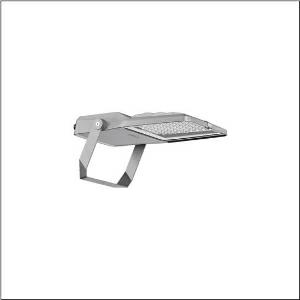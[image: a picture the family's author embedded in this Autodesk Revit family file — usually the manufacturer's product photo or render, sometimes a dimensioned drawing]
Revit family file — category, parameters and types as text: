
# Revit family: floodlight_fl_21_iq_mini___rs12_5xa7771b4b1a_1748
name_source: partatom
category: Lighting Fixtures
units: mm (PartAtom-declared; Revit-internal decimal feet)

## family parameters
Cut with Voids When Loaded = No
Host = Face
Light Source = No
Part Type = Normal
Room Calculation Point = No
Round Connector Dimension = Use Diameter
Shared = No

## types (1)
- --- (1 x LED, 6560 lm, 45.5 W, 4000K)
    Apparent Load = 46 VA
    CIE Flux Codes = 79 92 99 100 100
    Color Rendering = 70
    Color Temperature = 4000K
    Default Elevation = 1800 mm
    Description = Floodlight FL 21 iQ mini, floodlight, primary light control with lens, of PMMA, primary optical cover: protective disc, of toughened safety glass, transparent, light distribution: RS12, light emission: direct distribution, installation type: surface-mounted, LED, High Power LED, rated luminous flux: 6.560lm, luminous efficacy: 144lm/W, light colour: 740, colour temperature: 4000K, control gear: iQ Comfort/DALI, control: Auto-Match, Temp-Guard, Lumen-Switch, Night-Set, Smart-Wire, Light-Fading, Desk-Remote (wireless, voltage-free reading and setting of iQ features in the workshop via application-optimized NFC function/RFID function), optimised constant luminous flux control (CLO 2.0), with terminal, 6-pole, mains connection: 220..240V, AC, 50/60Hz, start of lifetime: 46W, end of service life: 48W, reduction: 22W, luminaire housing, of diecast aluminium, powder-coated, Siteco® metallic grey (DB 702S), corrosivity category C5 mid according to DIN EN ISO 12944, suitable for swimming pools, chlorine-resistant, sealing non-destructively replaceable, mounting bracket, of steel, galvanised, powder-coated, Siteco® metallic grey (DB 702S), protection rating (complete): IP66, insulation class (complete): insulation class II (safety insulation), certification: CE, ENEC, VDE, protection symbol: D, impact resistance: IK08, permissible operating ambient temperature: -40..+40°C, permissible operating ambient temperature for outdoor applications: -40..+50°C, standard: DIN EN 12944, LABS conformity tested according to VDMA 24364:2018-05, packaging unit: 1 piece

Light Distribution: RS12
    Height = 70 mm
    Lamp = 1 x LED
    Lamp Light Flux = 6560 lm
    Lamp Power = 45.5 W
    Lamp count = 1
    Length = 485 mm
    Luminous efficacy = 144 lm/W
    Manufacturer = Siteco
    ModVariant = No
    Model = 5XA7771B4B1A
    Mounting Place = Wall
    Mounting Type = Surface mounted
    Number of Poles = 1
    OnlyDefault = Yes
    Power Factor = 1
    Product Name = Floodlight FL 21 iQ mini | RS12
    Product group = floodlight | wall mounted
    ProductGroupID = 2001
    Protection Class = Protection class II
    Protection Degree = IP 66
    RLX_Detail_Level = 1
    RLX_Emergency_Light_Flux = 0 lm
    RLX_Emergency_Type = 0
    RLX_Emergency_Type_DB = No
    RlxData = <blob elided: 90909 chars, md5=3cedcb21>
    Socket = socket
    Standby Power = 0 W
    System Light Flux = 6560 lm
    System Power = 46 W
    Type Comments = factory setting: luminous flux: 100 % | dim-lin: 254 | 463 mA
    Type Image = l_1006845.jpg
    URL = http://relux.com
    VarID = @adj_167960
    Voltage = 0 V
    Weight = 0.00 kg
    Width = 337 mm

## geometry (parser evidence)
native form markers: Blend x4, Sweep x12
no freeform markers — native parametric forms only
